# Revit family: Railing_BlueWater_Safety-Rail-Seam-Grabber
name_source: partatom
category: Specialty Equipment
units: mm (PartAtom-declared; Revit-internal decimal feet)

## family parameters
Classification Number = 23.25.40.21.27
Cut with Voids When Loaded = No
Enable Cutting in Views = No
Maintain Annotation Orientation = No
Part Type = Normal
Room Calculation Point = No
Round Connector Dimension = Use Diameter
Shared = No

## types (9) — shared parameters
Assembly Code = C1010600
Building Codes = http://www.bluewater-mfg.com
Concentrated Load = 0.00 lbf
Construction Details = http://www.arcat.com
Default Elevation = 0' - 0"
Green Building-LEED = http://www.arcat.com
Horizontal Concentrated Load = 0.00 lbf/ft²
Installation-Fabrication = http://www.bluewater-mfg.com
Keynote = 05520
Manufacturer = BlueWater Mfg., Inc.
Mid-Rail Location = 1' - 9"
Post OD = 0' - 1 1/4"
Product Data = http://www.arcat.com
Product Properties = http://www.arcat.com
Rail OD = 0' - 1 1/4"
Railing Finish = Hot Dipped Galvanized
Railing Height = 3' - 6"
Railing Material = Steel - Hot Rolled Pickled Steel Tubing
Safety Standards = OSHA 29 CFR 1926.502 (b.) and 1910.23 (e.)
Sales Information = http://www.bluewater-mfg.com
Seam Plate Width = 1' - 0"
Specification = http://www.arcat.com
Type Comments = As Specified in the Contract Documents
URL = http://www.bluewater-mfg.com
Uniform Load = 0.00 lbf/ft
zero-valued in all types: Expected Lifespan (Years), Maintenance Schedule (Months), Warranty Duration (Years)

## per-type parameters (varying)
| type | Base Offset from Top Rail CL | Description | Mid Rail Offset | Model | Seam Plate Length | Upright Design |
| Curved Upright 30in Seam Spacing | 1' - 3" | BlueWater SafetyRail 2000 Guardrail System - Seam Grabber Series Guardrail with Curved Uprights as Specified | 0' - 11 1/2" | Architectural Series Guardrail Curved | 3' - 0" | SeamGrabberSeries : Curved Upright |
| Curved Upright 24in Seam Spacing | 1' - 3" | BlueWater SafetyRail 2000 Guardrail System - Seam Grabber Series Guardrail with Curved Uprights as Specified | 0' - 11 1/2" | Architectural Series Guardrail Curved | 2' - 6" | SeamGrabberSeries : Curved Upright |
| Curved Upright 18in Seam Spacing | 1' - 3" | BlueWater SafetyRail 2000 Guardrail System - Seam Grabber Series Guardrail with Curved Uprights as Specified | 0' - 11 1/2" | Architectural Series Guardrail Curved | 2' - 0" | SeamGrabberSeries : Curved Upright |
| Inclined Upright 30in Seam Spacing | 0' - 11 1/2" | BlueWater SafetyRail 2000 Guardrail System - Seam Grabber Series Guardrail with Inclined Uprights as Specified | 0' - 7 1/2" | Architectural Series Guardrail Inclined | 3' - 0" | SeamGrabberSeries : Incline Upright |
| Inclined Upright 24in Seam Spacing | 0' - 11 1/2" | BlueWater SafetyRail 2000 Guardrail System - Seam Grabber Series Guardrail with Inclined Uprights as Specified | 0' - 7 1/2" | Architectural Series Guardrail Inclined | 2' - 6" | SeamGrabberSeries : Incline Upright |
| Inclined Upright 18in Seam Spacing | 0' - 11 1/2" | BlueWater SafetyRail 2000 Guardrail System - Seam Grabber Series Guardrail with Inclined Uprights as Specified | 0' - 7 1/2" | Architectural Series Guardrail Inclined | 2' - 0" | SeamGrabberSeries : Incline Upright |
| Straight Upright 30in Seam Spacing | 0' - 0" | BlueWater SafetyRail 2000 Guardrail System - Seam Grabber Series Guardrail with Straight Uprights as Specified | 0' - 0" | Architectural Series Guardrail Straight | 3' - 0" | SeamGrabberSeries : Straight Upright |
| Straight Upright 24in Seam Spacing | 0' - 0" | BlueWater SafetyRail 2000 Guardrail System - Seam Grabber Series Guardrail with Straight Uprights as Specified | 0' - 0" | Architectural Series Guardrail Straight | 2' - 6" | SeamGrabberSeries : Straight Upright |
| Straight Upright 18in Seam Spacing | 0' - 0" | BlueWater SafetyRail 2000 Guardrail System - Seam Grabber Series Guardrail with Straight Uprights as Specified | 0' - 0" | Architectural Series Guardrail Straight | 2' - 0" | SeamGrabberSeries : Straight Upright |

## geometry (parser evidence)
native form markers: Sweep x5
no freeform markers — native parametric forms only
